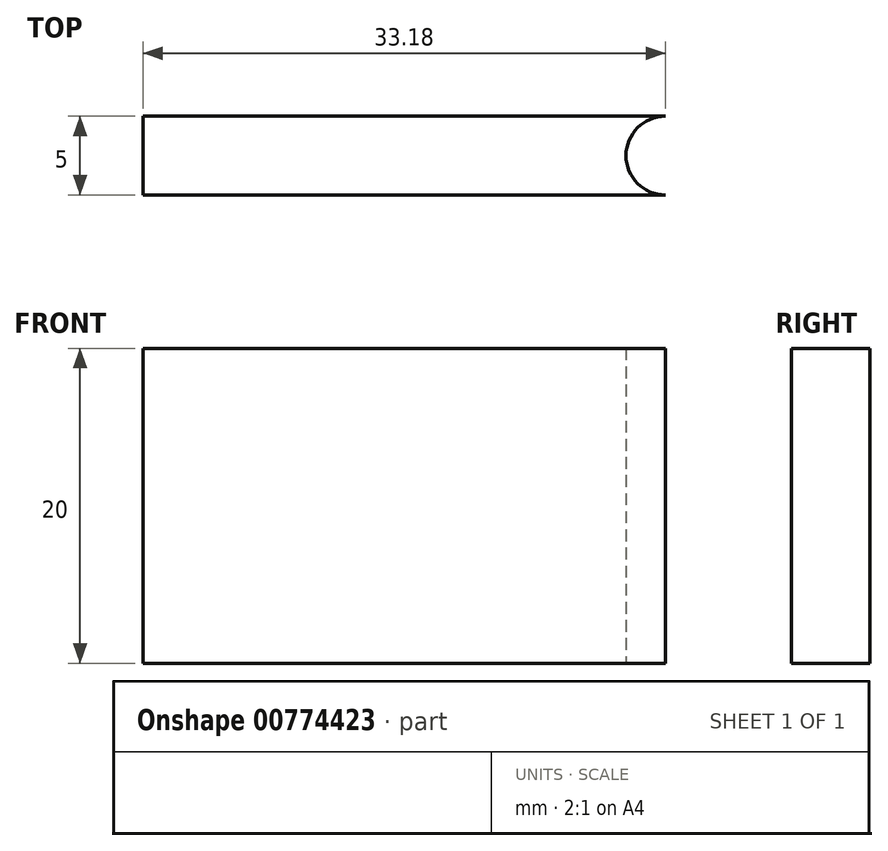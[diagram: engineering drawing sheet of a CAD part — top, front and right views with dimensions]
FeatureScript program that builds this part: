
annotation { "Feature Type Name" : "Feature", "Feature Type Description" : "" }
export const myFeature = defineFeature(function(context is Context, id is Id, definition is map)
    precondition{}
    {
        {
            var Q0;
            Q0=qCreatedBy(makeId("Top.planeOp"),FACE);
            var sketch = newSketch(context, id + "F0", { "sketchPlane" : qUnion([Q0])});
            skLineSegment(sketch, "E0.right", {"start": v(-42.16, -4.72) * mm, "end": v(-42.16, -9.72) * mm});
            skCircle(sketch, "E1", {"center": v(-8.98, -7.22) * mm, "radius": 2.5 * mm});
            skLineSegment(sketch, "E2", {"start": v(-42.16, -9.72) * mm, "end": v(-8.98, -9.72) * mm});
            skLineSegment(sketch, "E3", {"start": v(-42.16, -4.72) * mm, "end": v(-8.98, -4.72) * mm});
            skCircle(sketch, "E4.0", {"center": v(-8.98, -7.22) * mm, "radius": 1.5 * mm});
            skSolve(sketch);
        }
        {
            var Q0;
            Q0=makeQuery(id+"F0.imprint","IMPRINT",FACE,{"disambiguationData":[TD([[makeQuery(id+"F0.imprint","IMPRINT",EDGE,{"derivedFrom":sQuery(id+"F0.wireOp",EDGE,"E0.right")}),1.0]])]});
            extrude(context, id + "F1", {"entities" : qUnion([Q0]), "depth" : 20 * mm, "offsetDistance" : 25.4 * mm});
        }
    });
